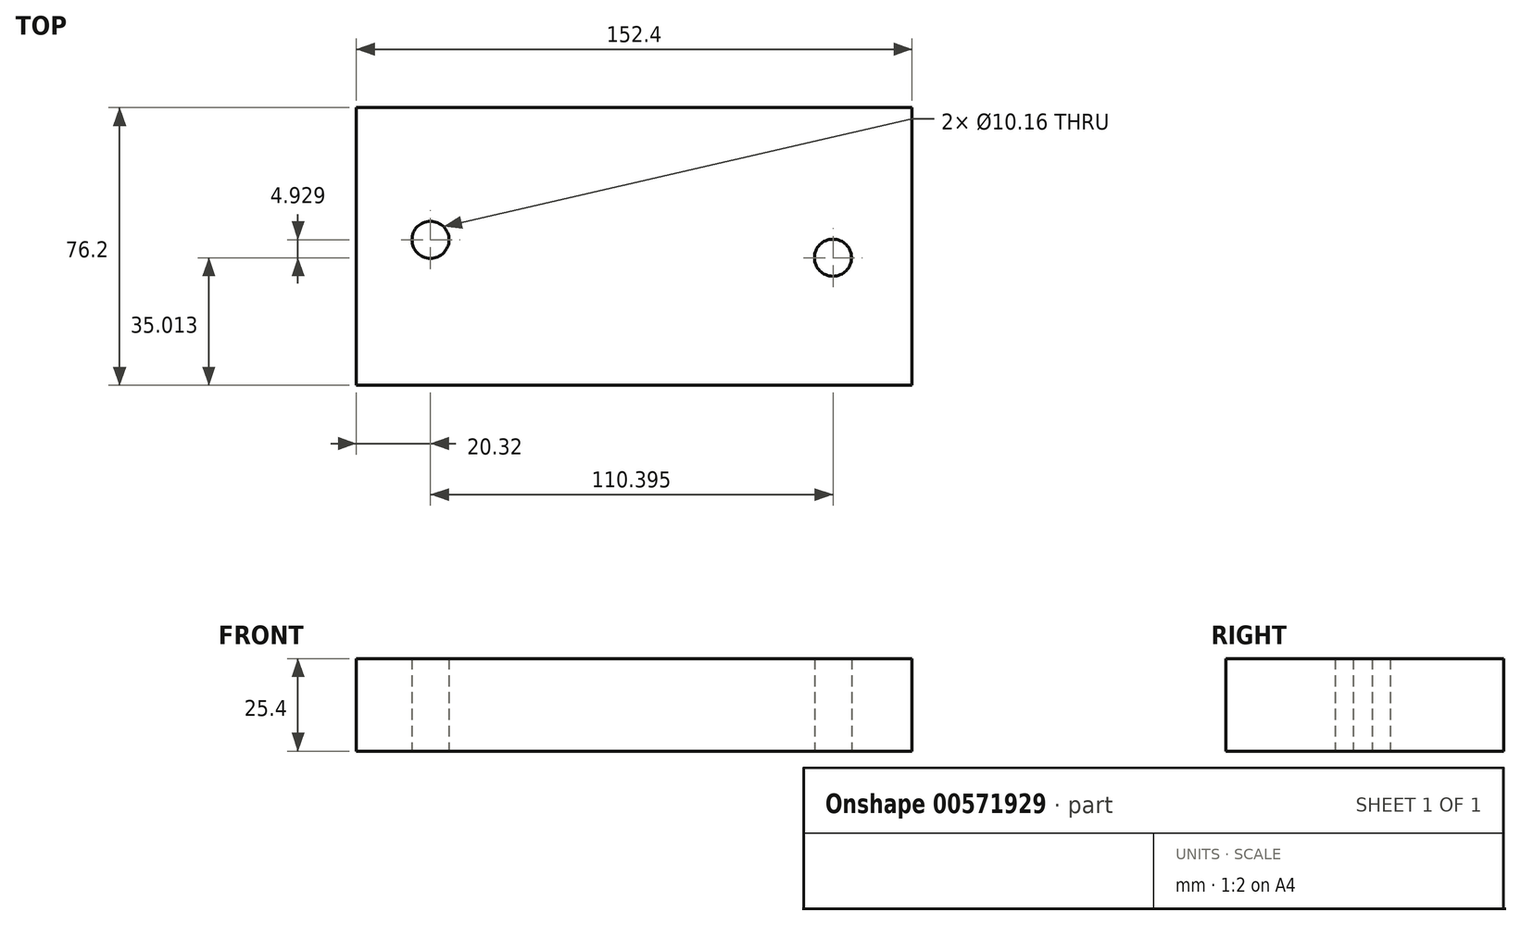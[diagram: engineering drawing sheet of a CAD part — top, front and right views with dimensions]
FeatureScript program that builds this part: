
annotation { "Feature Type Name" : "Feature", "Feature Type Description" : "" }
export const myFeature = defineFeature(function(context is Context, id is Id, definition is map)
    precondition{}
    {
        {
            var Q0;
            Q0=qCreatedBy(makeId("Top.planeOp"),FACE);
            var sketch = newSketch(context, id + "F0", { "sketchPlane" : qUnion([Q0])});
            skLineSegment(sketch, "E0.bottom", {"start": v(0, 0) * mm, "end": v(-152.4, 0) * mm});
            skLineSegment(sketch, "E0.top", {"start": v(0, -76.2) * mm, "end": v(-152.4, -76.2) * mm});
            skLineSegment(sketch, "E0.left", {"start": v(0, 0) * mm, "end": v(0, -76.2) * mm});
            skLineSegment(sketch, "E0.right", {"start": v(-152.4, 0) * mm, "end": v(-152.4, -76.2) * mm});
            skCircle(sketch, "E1", {"center": v(-132.08, -36.26) * mm, "radius": 5.08 * mm});
            skCircle(sketch, "E2", {"center": v(-21.69, -41.19) * mm, "radius": 5.08 * mm});
            skSolve(sketch);
        }
        {
            var Q0;
            Q0=makeQuery(id+"F0.imprint","IMPRINT",FACE,{"disambiguationData":[TD([[makeQuery(id+"F0.imprint","IMPRINT",EDGE,{"derivedFrom":sQuery(id+"F0.wireOp",EDGE,"E0.bottom")}),1.0]])]});
            extrude(context, id + "F1", {"entities" : qUnion([Q0]), "depth" : 25.4 * mm, "offsetDistance" : 25.4 * mm});
        }
    });
